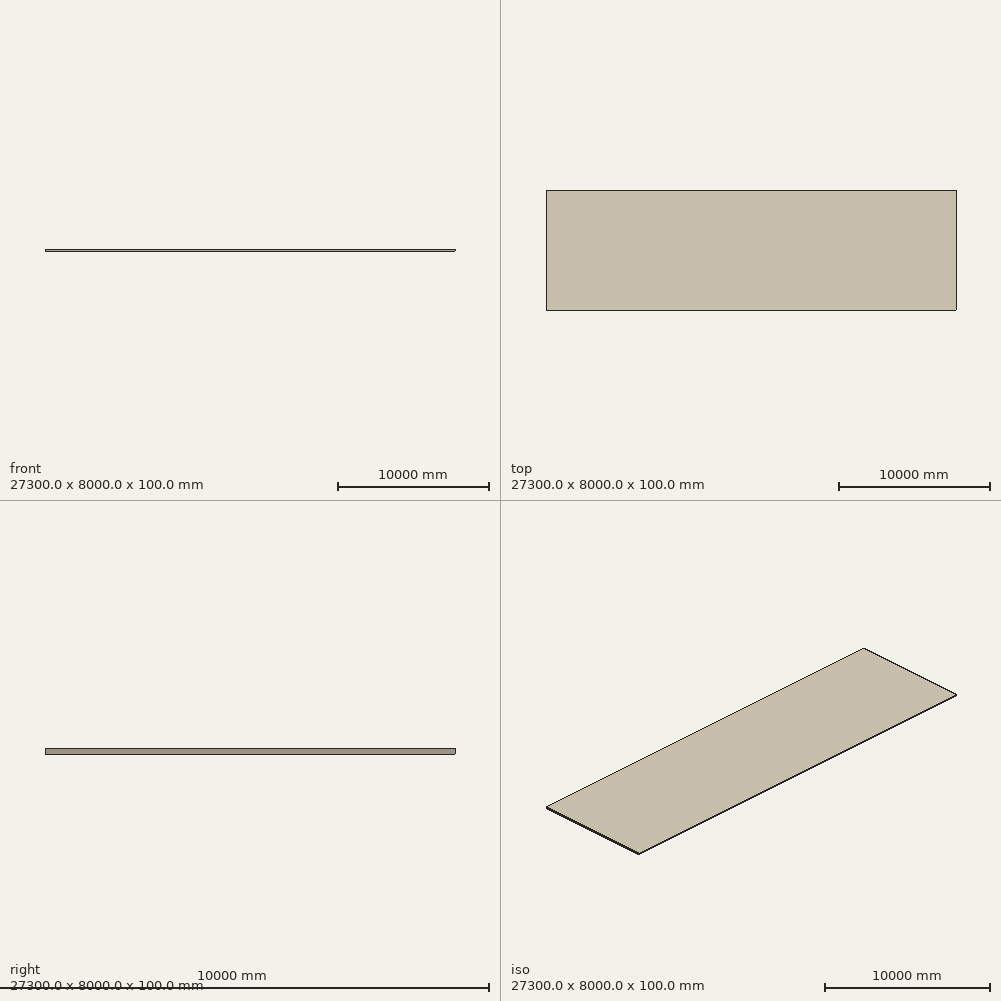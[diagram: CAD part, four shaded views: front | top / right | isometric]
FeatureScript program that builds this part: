
annotation { "Feature Type Name" : "Feature", "Feature Type Description" : "" }
export const myFeature = defineFeature(function(context is Context, id is Id, definition is map)
    precondition{}
    {
        {
            var Q0;
            Q0=qCreatedBy(makeId("Top.planeOp"),FACE);
            var sketch = newSketch(context, id + "F0", { "sketchPlane" : qUnion([Q0])});
            skLineSegment(sketch, "E0.bottom", {"start": v(-13604.53, 4213.46) * mm, "end": v(13695.47, 4213.46) * mm});
            skLineSegment(sketch, "E0.top", {"start": v(-13604.53, -3786.54) * mm, "end": v(13695.47, -3786.54) * mm});
            skLineSegment(sketch, "E0.left", {"start": v(-13604.53, 4213.46) * mm, "end": v(-13604.53, -3786.54) * mm});
            skLineSegment(sketch, "E0.right", {"start": v(13695.47, 4213.46) * mm, "end": v(13695.47, -3786.54) * mm});
            skSolve(sketch);
        }
        {
            var Q0;
            Q0=qSketchRegion(id+"F0",true);
            extrude(context, id + "F1", {"entities" : qUnion([Q0]), "depth" : 100 * mm});
        }
    });
